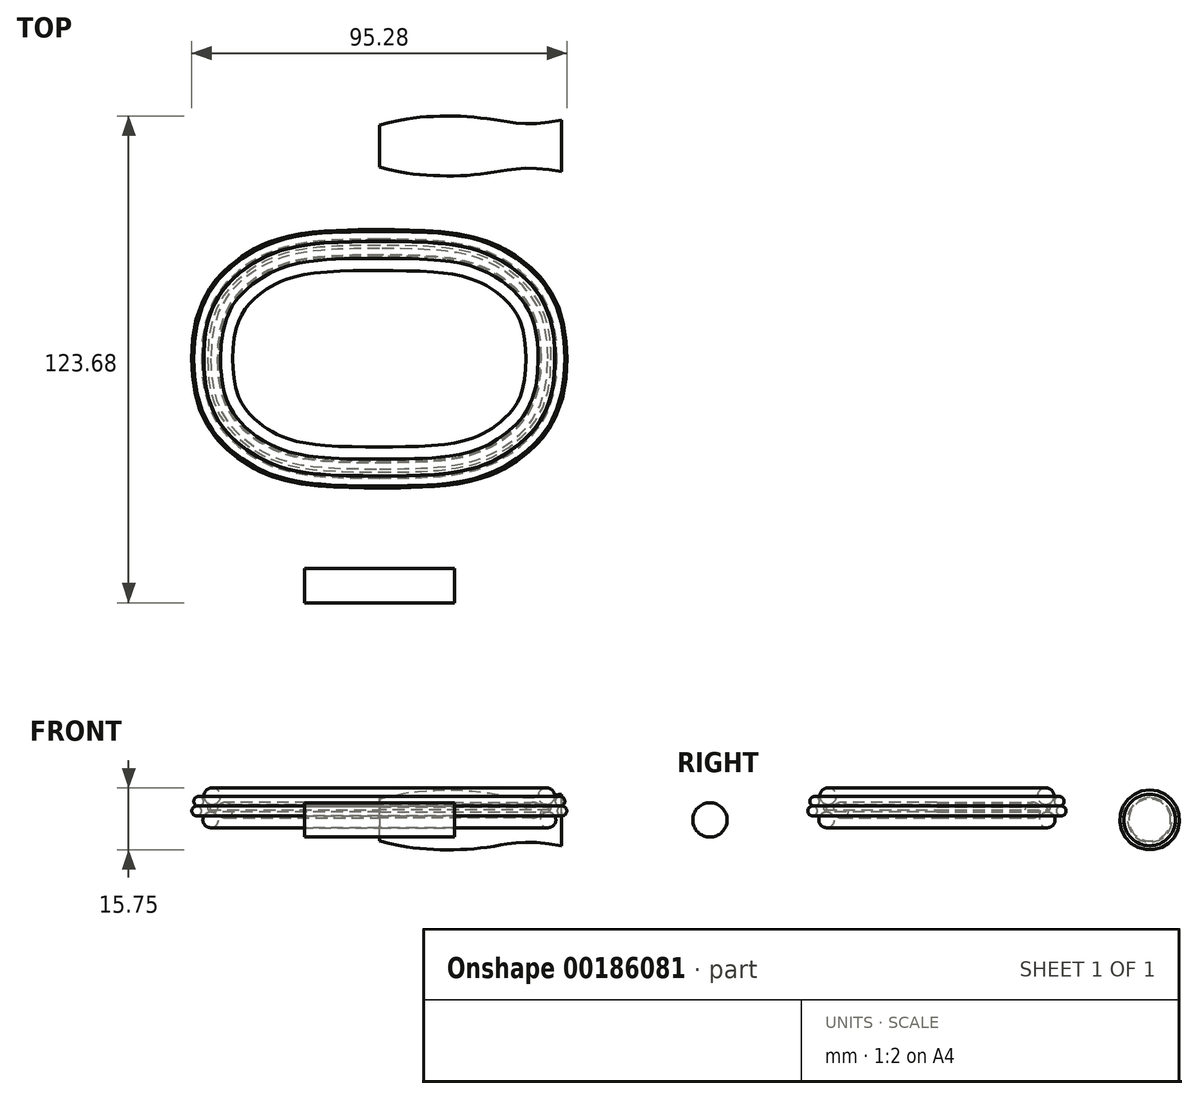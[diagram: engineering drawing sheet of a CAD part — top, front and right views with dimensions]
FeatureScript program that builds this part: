
annotation { "Feature Type Name" : "Feature", "Feature Type Description" : "" }
export const myFeature = defineFeature(function(context is Context, id is Id, definition is map)
    precondition{}
    {
        {
            var Q0;
            Q0=qCreatedBy(makeId("Right.planeOp"),FACE);
            var sketch = newSketch(context, id + "F0", { "sketchPlane" : qUnion([Q0])});
            skCircle(sketch, "E0", {"center": v(24.38, 2.48) * mm, "radius": 1.97 * mm});
            skCircle(sketch, "E1", {"center": v(27.63, 6.04) * mm, "radius": 2.11 * mm});
            skCircle(sketch, "E2", {"center": v(31.08, 4.72) * mm, "radius": 1.22 * mm});
            skCircle(sketch, "E3", {"center": v(28.03, 0) * mm, "radius": 1.98 * mm});
            skCircle(sketch, "E4", {"center": v(31.59, 2.28) * mm, "radius": 1.23 * mm});
            skCircle(sketch, "E5", {"center": v(28.4, 2.92) * mm, "radius": 0.4 * mm});
            skSolve(sketch);
        }
        {
            var Q0;
            Q0=qCreatedBy(makeId("Top.planeOp"),FACE);
            var sketch = newSketch(context, id + "F1", { "sketchPlane" : qUnion([Q0])});
            skFitSpline(sketch, "E6", {"points": [v(38.45, 0) * mm, v(32.46, 16.21) * mm, v(24.13, 21.3) * mm, v(0, 23.63) * mm], "startDerivative": vector(0, 83.3) * mm, "endDerivative": vector(-96.22, 0) * mm});
            skLineSegment(sketch, "E7", {"start": v(0, 23.63) * mm, "end": v(-15.88, 23.63) * mm, "construction": true});
            skLineSegment(sketch, "E8", {"start": v(38.45, 0) * mm, "end": v(38.45, -11.2) * mm, "construction": true});
            skFitSpline(sketch, "E9.MirrorCS", {"points": [v(38.45, 0) * mm, v(32.46, -16.21) * mm, v(24.13, -21.3) * mm, v(0, -23.63) * mm], "startDerivative": vector(0, -83.3) * mm, "endDerivative": vector(-96.22, 0) * mm});
            skFitSpline(sketch, "E10.MirrorCS", {"points": [v(-38.45, 0) * mm, v(-32.46, -16.21) * mm, v(-24.13, -21.3) * mm, v(0, -23.63) * mm], "startDerivative": vector(0, -83.3) * mm, "endDerivative": vector(96.22, 0) * mm});
            skFitSpline(sketch, "E11.MirrorCS", {"points": [v(-38.45, 0) * mm, v(-32.46, 16.21) * mm, v(-24.13, 21.3) * mm, v(0, 23.63) * mm], "startDerivative": vector(0, 83.3) * mm, "endDerivative": vector(96.22, 0) * mm});
            skSolve(sketch);
        }
        {
            var Q0;
            Q0 = qSketchRegion(id + "F0", true);
            var Q1;
            Q1 = qConstructionFilter(qBodyType(qCreatedBy(id + "F1" ,EDGE), BodyType.WIRE), ConstructionObject.NO);
            sweep(context, id + "F2", {"profiles" : qUnion([Q0]), "path" : qUnion([Q1])});
        }
        {
            var Q0;
            Q0=qCreatedBy(makeId("Top.planeOp"),FACE);
            var sketch = newSketch(context, id + "F3", { "sketchPlane" : qUnion([Q0])});
            skLineSegment(sketch, "E12", {"start": v(0, 54.06) * mm, "end": v(46.28, 54.06) * mm});
            skLineSegment(sketch, "E13", {"start": v(0, 54.06) * mm, "end": v(0, 59.37) * mm});
            skFitSpline(sketch, "E14", {"points": [v(0, 59.37) * mm, v(7.87, 61.06) * mm, v(24, 61.39) * mm, v(36.95, 59.74) * mm, v(46.28, 60.6) * mm], "startDerivative": vector(33.48, 8.98) * mm, "endDerivative": vector(40.13, 6.6) * mm});
            skLineSegment(sketch, "E15", {"start": v(46.28, 60.6) * mm, "end": v(46.28, 54.06) * mm});
            skSolve(sketch);
        }
        {
            var Q0;
            Q0 = qSketchRegion(id + "F3", true);
            var Q1;
            Q1=sQuery(id+"F3.wireOp",EDGE,"E12");
            revolve(context, id + "F4", {"surfaceOperationType" : NewSurfaceOperationType.NEW, "entities" : qUnion([Q0]), "axis" : qUnion([Q1]), "revolveType" : RevolveType.FULL});
        }
        {
            var Q0;
            Q0=qCreatedBy(makeId("Right.planeOp"),FACE);
            var sketch = newSketch(context, id + "F5", { "sketchPlane" : qUnion([Q0])});
            skCircle(sketch, "E16", {"center": v(-57.66, 0) * mm, "radius": 4.36 * mm});
            skSolve(sketch);
        }
        {
            var Q0;
            Q0=makeQuery(id+"F5.imprint","IMPRINT",FACE,{"disambiguationData":[TD([[makeQuery(id+"F5.imprint","IMPRINT",EDGE,{"derivedFrom":sQuery(id+"F5.wireOp",EDGE,"E16")}),1.0]])]});
            extrude(context, id + "F6", {"entities" : qUnion([Q0]), "endBound" : BoundingType.SYMMETRIC, "depth" : 38.1 * mm});
        }
    });
